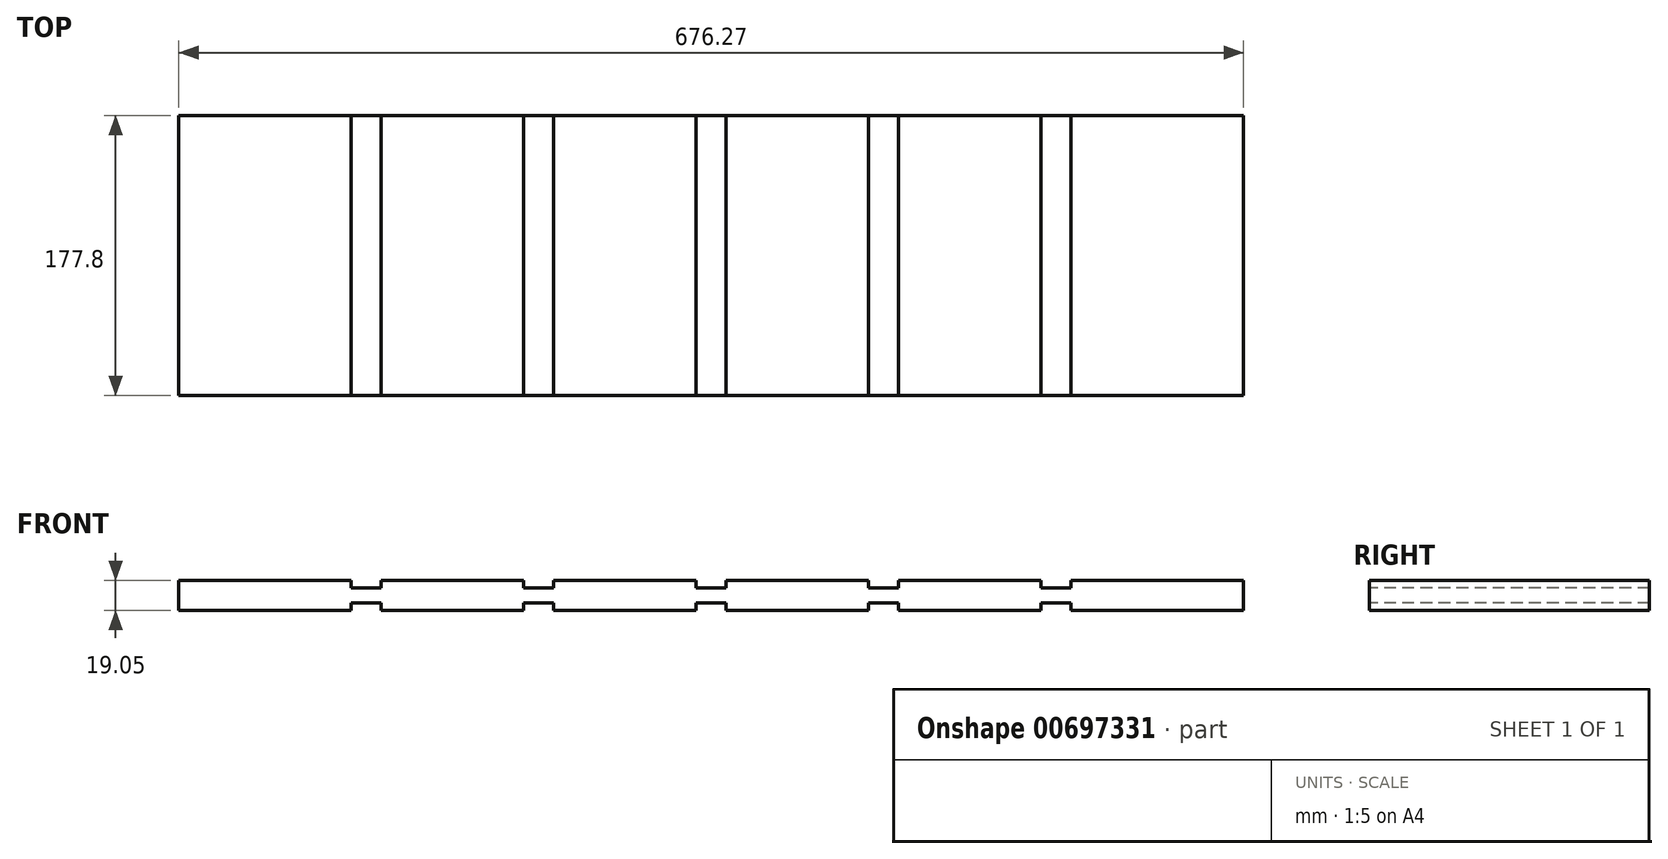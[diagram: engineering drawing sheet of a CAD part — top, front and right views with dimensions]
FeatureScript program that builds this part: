
annotation { "Feature Type Name" : "Feature", "Feature Type Description" : "" }
export const myFeature = defineFeature(function(context is Context, id is Id, definition is map)
    precondition{}
    {
        {
            var Q0;
            Q0=qCreatedBy(makeId("Front.planeOp"),FACE);
            var sketch = newSketch(context, id + "F0", { "sketchPlane" : qUnion([Q0])});
            skLineSegment(sketch, "E0.bottom", {"start": v(0, 0) * mm, "end": v(676.28, 0) * mm});
            skLineSegment(sketch, "E0.top", {"start": v(0, 19.05) * mm, "end": v(676.28, 19.05) * mm});
            skLineSegment(sketch, "E0.left", {"start": v(0, 0) * mm, "end": v(0, 19.05) * mm});
            skLineSegment(sketch, "E0.right", {"start": v(676.28, 0) * mm, "end": v(676.28, 19.05) * mm});
            skSolve(sketch);
        }
        {
            var Q0;
            Q0=qCreatedBy(makeId("Front.planeOp"),FACE);
            var sketch = newSketch(context, id + "F1", { "sketchPlane" : qUnion([Q0])});
            skLineSegment(sketch, "E1.bottom", {"start": v(109.54, 0) * mm, "end": v(128.59, 0) * mm});
            skLineSegment(sketch, "E1.top", {"start": v(109.54, 4.76) * mm, "end": v(128.59, 4.76) * mm});
            skLineSegment(sketch, "E1.left", {"start": v(109.54, 0) * mm, "end": v(109.54, 4.76) * mm});
            skLineSegment(sketch, "E1.right", {"start": v(128.59, 0) * mm, "end": v(128.59, 4.76) * mm});
            skLineSegment(sketch, "E2.0.1.0", {"start": v(109.54, 19.05) * mm, "end": v(128.59, 19.05) * mm});
            skLineSegment(sketch, "E2.0.1.1", {"start": v(109.54, 14.29) * mm, "end": v(128.59, 14.29) * mm});
            skLineSegment(sketch, "E2.0.1.2", {"start": v(109.54, 14.29) * mm, "end": v(109.54, 19.05) * mm});
            skLineSegment(sketch, "E2.0.1.3", {"start": v(128.59, 14.29) * mm, "end": v(128.59, 19.05) * mm});
            skLineSegment(sketch, "E2.1.0.0", {"start": v(219.08, 4.76) * mm, "end": v(238.13, 4.76) * mm});
            skLineSegment(sketch, "E2.1.0.1", {"start": v(219.08, 0) * mm, "end": v(238.13, 0) * mm});
            skLineSegment(sketch, "E2.1.0.2", {"start": v(219.08, 0) * mm, "end": v(219.08, 4.76) * mm});
            skLineSegment(sketch, "E2.1.0.3", {"start": v(238.13, 0) * mm, "end": v(238.13, 4.76) * mm});
            skLineSegment(sketch, "E2.1.1.0", {"start": v(219.08, 19.05) * mm, "end": v(238.13, 19.05) * mm});
            skLineSegment(sketch, "E2.1.1.1", {"start": v(219.08, 14.29) * mm, "end": v(238.13, 14.29) * mm});
            skLineSegment(sketch, "E2.1.1.2", {"start": v(219.08, 14.29) * mm, "end": v(219.08, 19.05) * mm});
            skLineSegment(sketch, "E2.1.1.3", {"start": v(238.13, 14.29) * mm, "end": v(238.13, 19.05) * mm});
            skLineSegment(sketch, "E2.2.0.0", {"start": v(328.61, 4.76) * mm, "end": v(347.66, 4.76) * mm});
            skLineSegment(sketch, "E2.2.0.1", {"start": v(328.61, 0) * mm, "end": v(347.66, 0) * mm});
            skLineSegment(sketch, "E2.2.0.2", {"start": v(328.61, 0) * mm, "end": v(328.61, 4.76) * mm});
            skLineSegment(sketch, "E2.2.0.3", {"start": v(347.66, 0) * mm, "end": v(347.66, 4.76) * mm});
            skLineSegment(sketch, "E2.2.1.0", {"start": v(328.61, 19.05) * mm, "end": v(347.66, 19.05) * mm});
            skLineSegment(sketch, "E2.2.1.1", {"start": v(328.61, 14.29) * mm, "end": v(347.66, 14.29) * mm});
            skLineSegment(sketch, "E2.2.1.2", {"start": v(328.61, 14.29) * mm, "end": v(328.61, 19.05) * mm});
            skLineSegment(sketch, "E2.2.1.3", {"start": v(347.66, 14.29) * mm, "end": v(347.66, 19.05) * mm});
            skLineSegment(sketch, "E2.3.0.0", {"start": v(438.15, 4.76) * mm, "end": v(457.2, 4.76) * mm});
            skLineSegment(sketch, "E2.3.0.1", {"start": v(438.15, 0) * mm, "end": v(457.2, 0) * mm});
            skLineSegment(sketch, "E2.3.0.2", {"start": v(438.15, 0) * mm, "end": v(438.15, 4.76) * mm});
            skLineSegment(sketch, "E2.3.0.3", {"start": v(457.2, 0) * mm, "end": v(457.2, 4.76) * mm});
            skLineSegment(sketch, "E2.3.1.0", {"start": v(438.15, 19.05) * mm, "end": v(457.2, 19.05) * mm});
            skLineSegment(sketch, "E2.3.1.1", {"start": v(438.15, 14.29) * mm, "end": v(457.2, 14.29) * mm});
            skLineSegment(sketch, "E2.3.1.2", {"start": v(438.15, 14.29) * mm, "end": v(438.15, 19.05) * mm});
            skLineSegment(sketch, "E2.3.1.3", {"start": v(457.2, 14.29) * mm, "end": v(457.2, 19.05) * mm});
            skLineSegment(sketch, "E2.4.0.0", {"start": v(547.69, 4.76) * mm, "end": v(566.74, 4.76) * mm});
            skLineSegment(sketch, "E2.4.0.1", {"start": v(547.69, 0) * mm, "end": v(566.74, 0) * mm});
            skLineSegment(sketch, "E2.4.0.2", {"start": v(547.69, 0) * mm, "end": v(547.69, 4.76) * mm});
            skLineSegment(sketch, "E2.4.0.3", {"start": v(566.74, 0) * mm, "end": v(566.74, 4.76) * mm});
            skLineSegment(sketch, "E2.4.1.0", {"start": v(547.69, 19.05) * mm, "end": v(566.74, 19.05) * mm});
            skLineSegment(sketch, "E2.4.1.1", {"start": v(547.69, 14.29) * mm, "end": v(566.74, 14.29) * mm});
            skLineSegment(sketch, "E2.4.1.2", {"start": v(547.69, 14.29) * mm, "end": v(547.69, 19.05) * mm});
            skLineSegment(sketch, "E2.4.1.3", {"start": v(566.74, 14.29) * mm, "end": v(566.74, 19.05) * mm});
            skLineSegment(sketch, "E2.direction1", {"start": v(109.54, 0) * mm, "end": v(219.08, 0) * mm, "construction": true});
            skLineSegment(sketch, "E2.direction2", {"start": v(109.54, 0) * mm, "end": v(109.54, 14.29) * mm, "construction": true});
            skSolve(sketch);
        }
        {
            var Q0;
            Q0=qSketchRegion(id+"F0",true);
            extrude(context, id + "F2", {"entities" : qUnion([Q0]), "oppositeDirection" : true, "depth" : 177.8 * mm, "offsetDistance" : 25.4 * mm});
        }
        {
            var Q0;
            Q0=qSketchRegion(id+"F1",true);
            extrude(context, id + "F3", {"entities" : qUnion([Q0]), "operationType" : NewBodyOperationType.REMOVE, "endBound" : BoundingType.THROUGH_ALL, "oppositeDirection" : true, "depth" : 25.4 * mm, "offsetDistance" : 25.4 * mm});
        }
    });
